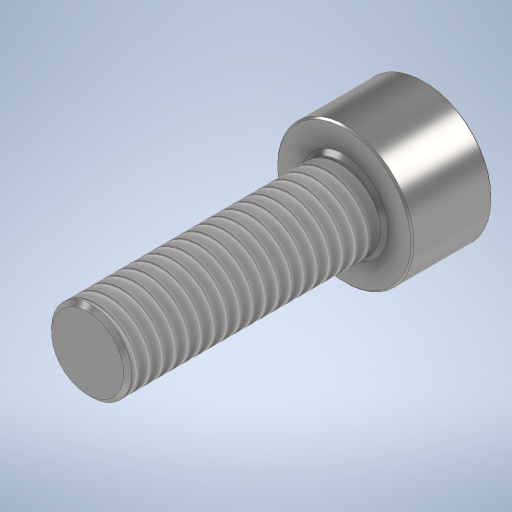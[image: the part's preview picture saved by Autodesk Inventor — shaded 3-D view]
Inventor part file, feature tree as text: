
AUTODESK INVENTOR PART (.ipt)
format: ipt  version: 2024 (Build 280153000, 153)  size: 331,264 bytes
history: native  units: mm
features: extrude x3, chamfer x3, sketch x2, thread x1, hole x1
ambient origin geometry x8: Origin, YZ Plane, XZ Plane, XY Plane, X Axis, Y Axis, Z Axis, Center Point
bodies: Solid1 (feature_tree)
feature tree (10):
  sketch  "Sketch1"  dims[d0=8.5mm d1=5.0mm]
  extrude  "Extrusion1"  Depth=5.0mm
  extrude  "Extrusion2"  Depth=2.5mm TaperAngle=0.0deg
  thread  "Thread1"  [1 undecoded]
  chamfer  "Chamfer1"  Distance=0.1mm Angle=45.0deg
  sketch  "Sketch2"  dims[d2=16.0mm d3=0.0mm d4=5.0mm d5=0.0mm d6=15.0mm d7=0.0mm d8=0.1mm d9=2.0mm d10=45.0deg d11=3.75mm d12=4.0mm d15=0.5mm d16=2.0mm d17=45.0deg d18=3.0mm d19=0.0mm d20=0.25mm d21=2.0mm d22=45.0deg d23=3.75mm d24=6.0mm d25=4.0mm d26=2.0mm d27=90.0deg d28=2.5mm d29=150.0deg]
  hole  "Hole1"  [1 undecoded]
  chamfer  "Chamfer2"  Distance=4.0mm
  extrude  "Extrusion4"  Depth=2.5mm TaperAngle=45.0deg
  chamfer  "Chamfer3"  Distance=3.0mm
note: 2 required parameter values undecoded (feature->parameter linkage not recoverable at this tier; creation-order binding heuristic only, values carry confidence <= 0.55)
